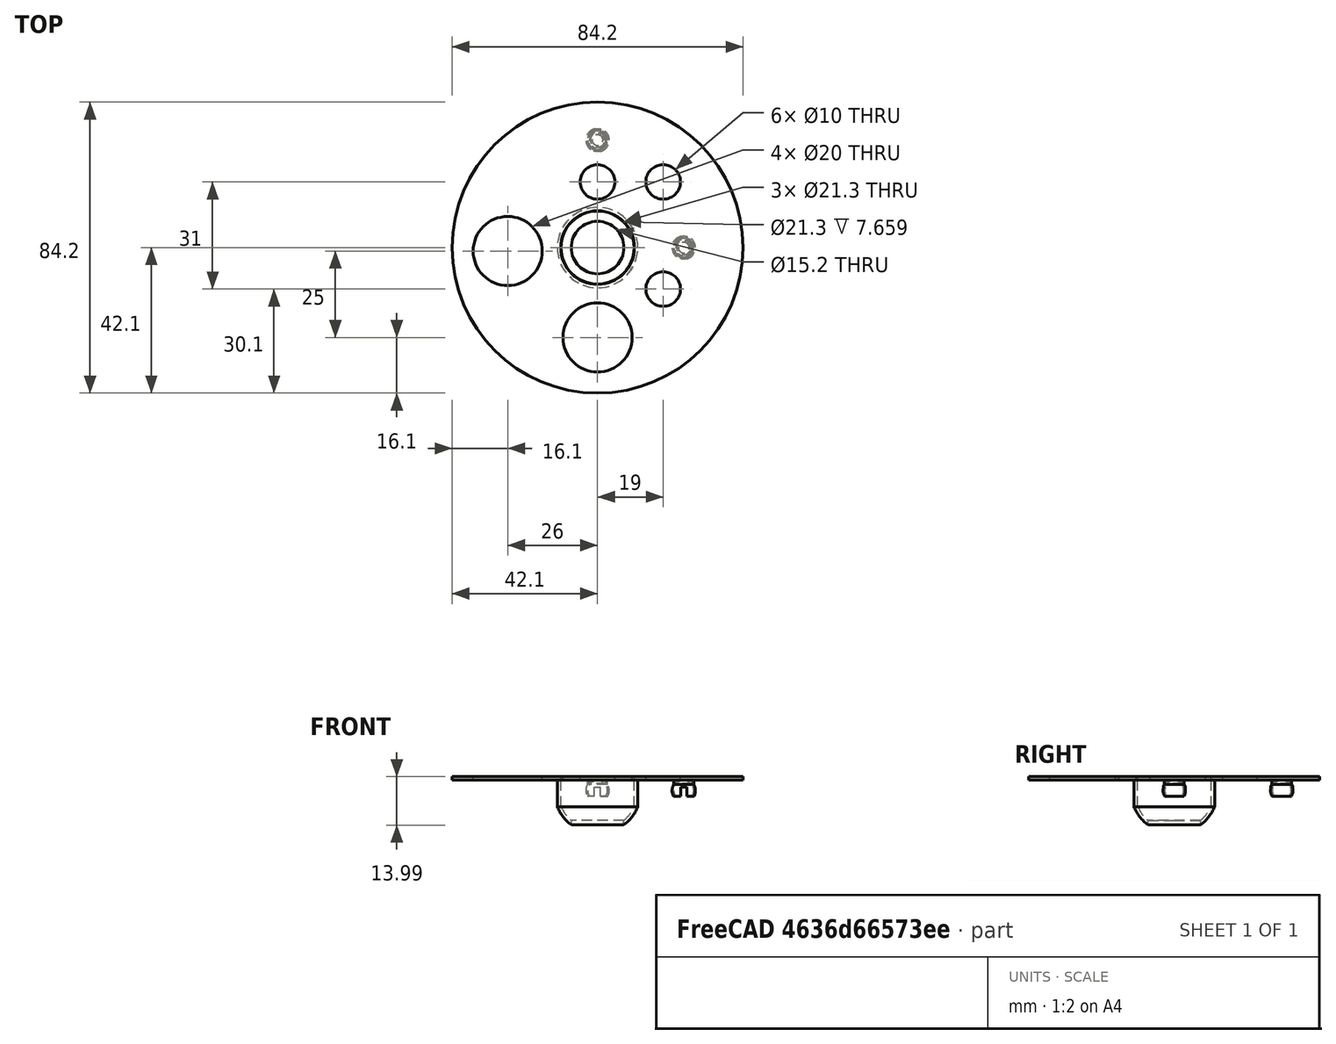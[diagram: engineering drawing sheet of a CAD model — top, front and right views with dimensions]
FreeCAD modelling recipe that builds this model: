
FCSTD DOCUMENT  (FreeCAD 0.18R16131 (Git))
Label: retrovisor
License: All rights reserved
LicenseURL: http://en.wikipedia.org/wiki/All_rights_reserved
objects: Part::Cut×23, Part::Cylinder×21, Part::Sphere×7, Part::Box×2, Part::MultiFuse×2
note: 55 computed .brp shape members not serialized (recipe doc carries the construction recipe); baked Part::Feature solids carry a one-line shape summary decoded from their .brp

FEATURE [Part::Sphere] Sphere
  Angle1 = -90
  Angle2 = -21.79
  Angle3 = 360
  AttacherType = Attacher::AttachEngine3D
  Radius = 12.55
FEATURE [Part::Sphere] Sphere001
  Angle1 = -90
  Angle2 = 90
  Angle3 = 360
  AttacherType = Attacher::AttachEngine3D
  Radius = 11.55
FEATURE [Part::Cut] Cut
  Base = -> Sphere
  Tool = -> Sphere001
FEATURE [Part::Cylinder] Cylinder
  Angle = 360
  AttacherType = Attacher::AttachEngine3D
  Height = 7.96
  Placement = pos=(0,0,-4.7) rot=(0,0,1;0rad)
  Radius = 11.65
FEATURE [Part::Cylinder] Cylinder001
  Angle = 360
  AttacherType = Attacher::AttachEngine3D
  Height = 10
  Placement = pos=(0,0,-5) rot=(0,0,1;0rad)
  Radius = 10.65
FEATURE [Part::Cut] Cut001  label="altura"
  Base = -> Cylinder
  Tool = -> Cylinder001
FEATURE [Part::Cylinder] Cylinder002  label="Cilindro"
  Angle = 360
  AttacherType = Attacher::AttachEngine3D
  Height = 1
  Placement = pos=(0,0,5) rot=(0,0,1;0rad)
  Radius = 42.1
FEATURE [Part::Cylinder] Cylinder003  label="Cilindro001"
  Angle = 360
  AttacherType = Attacher::AttachEngine3D
  Height = 10
  Radius = 10.65
FEATURE [Part::Cut] Cut002  label="plataforma"
  Base = -> Cylinder002
  Placement = pos=(0,0,-2) rot=(0,0,1;0rad)
  Tool = -> Cylinder003
FEATURE [Part::Cylinder] Cylinder004  label="Cilindro002"
  Angle = 360
  AttacherType = Attacher::AttachEngine3D
  Height = 10
  Placement = pos=(0,0,-17) rot=(0,0,1;0rad)
  Radius = 7.6
FEATURE [Part::Cut] Cut003  label="base"
  Base = -> Cut
  Tool = -> Cylinder004
FEATURE [Part::Sphere] Sphere002  label="Esfera"
  Angle1 = -90
  Angle2 = 30
  Angle3 = 360
  AttacherType = Attacher::AttachEngine3D
  Radius = 3.38
FEATURE [Part::Sphere] Sphere003  label="Esfera001"
  Angle1 = -90
  Angle2 = 90
  Angle3 = 360
  AttacherType = Attacher::AttachEngine3D
  Radius = 2.88
FEATURE [Part::Box] Box  label="Cubo"
  AttacherType = Attacher::AttachEngine3D
  Height = 10
  Length = 1.81
  Placement = pos=(-0.91,-4,-1) rot=(0,0,1;0rad)
  Width = 10
FEATURE [Part::Cut] Cut004
  Base = -> Sphere002
  Tool = -> Sphere003
FEATURE [Part::Cut] Cut005  label="gorroTornillo"
  Base = -> Cut004
  Placement = pos=(24.95,0,0) rot=(1,0,0;3.14159rad)
  Tool = -> Box
FEATURE [Part::Sphere] Sphere004  label="Esfera002"
  Angle1 = -90
  Angle2 = 90
  Angle3 = 360
  AttacherType = Attacher::AttachEngine3D
  Radius = 2.88
FEATURE [Part::Sphere] Sphere005  label="Esfera003"
  Angle1 = -90
  Angle2 = 30
  Angle3 = 360
  AttacherType = Attacher::AttachEngine3D
  Radius = 3.38
FEATURE [Part::Box] Box001  label="Cubo001"
  AttacherType = Attacher::AttachEngine3D
  Height = 10
  Length = 1.81
  Placement = pos=(-0.91,-4,-1) rot=(0,0,1;0rad)
  Width = 10
FEATURE [Part::Cut] Cut007
  Base = -> Sphere005
  Tool = -> Sphere004
FEATURE [Part::Cut] Cut006  label="gorroTornillo001"
  Base = -> Cut007
  Placement = pos=(0,31.1,0) rot=(1,0,0;3.14159rad)
  Tool = -> Box001
FEATURE [Part::Cylinder] Cylinder005  label="Cilindro003"
  Angle = 360
  AttacherType = Attacher::AttachEngine3D
  Height = 10
  Placement = pos=(0,19,0) rot=(0,0,1;0rad)
  Radius = 5
FEATURE [Part::Cylinder] Cylinder006  label="Cilindro004"
  Angle = 360
  AttacherType = Attacher::AttachEngine3D
  Height = 10
  Placement = pos=(0,-26,0) rot=(0,0,1;0rad)
  Radius = 10
FEATURE [Part::Cylinder] Cylinder007  label="Cilindro005"
  Angle = 360
  AttacherType = Attacher::AttachEngine3D
  Height = 10
  Placement = pos=(-26,-1,0) rot=(0,0,1;0rad)
  Radius = 10
FEATURE [Part::Cylinder] Cylinder008  label="Cilindro006"
  Angle = 360
  AttacherType = Attacher::AttachEngine3D
  Height = 10
  Placement = pos=(19,-12,0) rot=(0,0,1;0rad)
  Radius = 5
FEATURE [Part::Cylinder] Cylinder009  label="Cilindro007"
  Angle = 360
  AttacherType = Attacher::AttachEngine3D
  Height = 10
  Placement = pos=(19,19,0) rot=(0,0,1;0rad)
  Radius = 5
FEATURE [Part::Cut] Cut008
  Base = -> Cut002
  Tool = -> Cylinder005
FEATURE [Part::Cut] Cut009
  Base = -> Cut008
  Tool = -> Cylinder009
FEATURE [Part::Cut] Cut010
  Base = -> Cut009
  Tool = -> Cylinder008
FEATURE [Part::Cut] Cut011
  Base = -> Cut010
  Tool = -> Cylinder007
FEATURE [Part::Cut] Cut012  label="plataforma001"
  Base = -> Cut011
  Tool = -> Cylinder006
FEATURE [Part::MultiFuse] Fusion
  Shapes = -> [Cut001,Cut003,Cut006,Cut005,Cut012]
FEATURE [Part::Cylinder] Cylinder011  label="Cilindro009"
  Angle = 360
  AttacherType = Attacher::AttachEngine3D
  Height = 10
  Radius = 2.88
FEATURE [Part::Cut] Cut013
  Base = -> Cylinder011
  Placement = pos=(0,31.1,1) rot=(0,0,1;0rad)
  Tool = -> Sphere004
FEATURE [Part::Cylinder] Cylinder012  label="Cilindro010"
  Angle = 360
  AttacherType = Attacher::AttachEngine3D
  Height = 10
  Radius = 2.88
FEATURE [Part::Sphere] Sphere006  label="Esfera004"
  Angle1 = -90
  Angle2 = 90
  Angle3 = 360
  AttacherType = Attacher::AttachEngine3D
  Radius = 2.88
FEATURE [Part::Cut] Cut014
  Base = -> Cylinder012
  Placement = pos=(24.95,0,1) rot=(0,0,1;0rad)
  Tool = -> Sphere006
FEATURE [Part::Cylinder] Cylinder013  label="Cilindro011"
  Angle = 360
  AttacherType = Attacher::AttachEngine3D
  Height = 10
  Placement = pos=(0,19,0) rot=(0,0,1;0rad)
  Radius = 5
FEATURE [Part::Cylinder] Cylinder015  label="Cilindro013"
  Angle = 360
  AttacherType = Attacher::AttachEngine3D
  Height = 10
  Radius = 10.65
FEATURE [Part::Cylinder] Cylinder016  label="Cilindro014"
  Angle = 360
  AttacherType = Attacher::AttachEngine3D
  Height = 10
  Placement = pos=(19,-12,0) rot=(0,0,1;0rad)
  Radius = 5
FEATURE [Part::Cylinder] Cylinder017  label="Cilindro015"
  Angle = 360
  AttacherType = Attacher::AttachEngine3D
  Height = 10
  Placement = pos=(19,19,0) rot=(0,0,1;0rad)
  Radius = 5
FEATURE [Part::Cylinder] Cylinder019  label="Cilindro017"
  Angle = 360
  AttacherType = Attacher::AttachEngine3D
  Height = 1
  Placement = pos=(0,0,5) rot=(0,0,1;0rad)
  Radius = 42.1
FEATURE [Part::Cut] Cut019  label="plataforma002"
  Base = -> Cylinder019
  Placement = pos=(0,0,-2) rot=(0,0,1;0rad)
  Tool = -> Cylinder015
FEATURE [Part::Cut] Cut015
  Base = -> Cut019
  Tool = -> Cylinder013
FEATURE [Part::Cut] Cut018
  Base = -> Cut015
  Tool = -> Cylinder017
FEATURE [Part::Cut] Cut016
  Base = -> Cut018
  Tool = -> Cylinder016
FEATURE [Part::Cylinder] Cylinder018  label="Cilindro016"
  Angle = 360
  AttacherType = Attacher::AttachEngine3D
  Height = 10
  Placement = pos=(-26,-1,0) rot=(0,0,1;0rad)
  Radius = 10
FEATURE [Part::Cut] Cut017
  Base = -> Cut016
  Tool = -> Cylinder018
FEATURE [Part::Cylinder] Cylinder014  label="Cilindro012"
  Angle = 360
  AttacherType = Attacher::AttachEngine3D
  Height = 10
  Placement = pos=(0,-26,0) rot=(0,0,1;0rad)
  Radius = 10
FEATURE [Part::Cut] Cut020  label="plataforma003"
  Base = -> Cut017
  Tool = -> Cylinder014
FEATURE [Part::Cylinder] Cylinder020  label="Cilindro018"
  Angle = 360
  AttacherType = Attacher::AttachEngine3D
  Height = 7
  Placement = pos=(0,31.1,4) rot=(0,0,1;0rad)
  Radius = 2.88
FEATURE [Part::Cylinder] Cylinder021  label="Cilindro019"
  Angle = 360
  AttacherType = Attacher::AttachEngine3D
  Height = 7
  Placement = pos=(24.95,0,4) rot=(0,0,1;0rad)
  Radius = 2.88
FEATURE [Part::Cut] Cut021
  Base = -> Cut014
  Tool = -> Cylinder021
FEATURE [Part::Cut] Cut022
  Base = -> Cut013
  Tool = -> Cylinder020
FEATURE [Part::MultiFuse] Fusion001
  Shapes = -> [Fusion,Cut021,Cut022]
